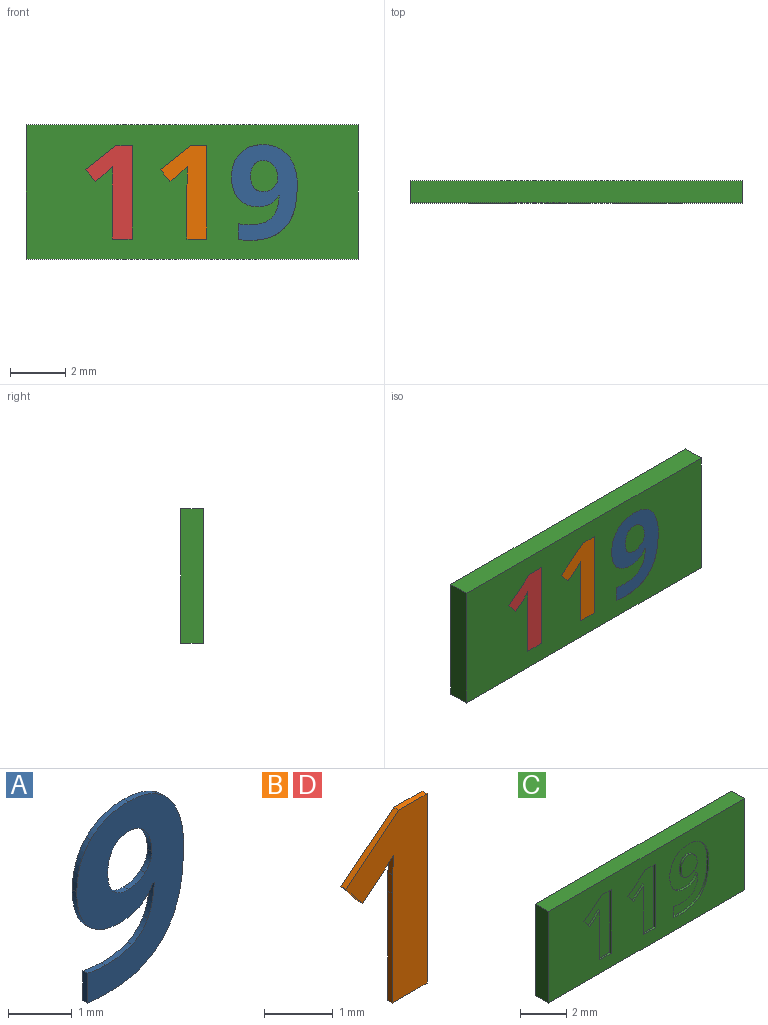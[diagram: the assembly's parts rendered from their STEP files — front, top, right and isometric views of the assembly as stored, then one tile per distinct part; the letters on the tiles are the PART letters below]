
ASSEMBLY  parts=4 mates=3
PART A: 28 faces, bbox 2.4x0.1x3.5 mm
  f0: plane 3.46x2.38mm, normal (0,-1,0), area 4.8mm2, adj f1,f2,f3,f4,f5,f6,f7,f8
  f1: extruded ~0.51x0.43mm, area 0.1mm2, adj f0,f2,f21,f23
  f2: extruded ~0.65x0.18mm, area 0.1mm2, adj f0,f1,f3,f21
  f3: extruded ~0.84x0.31mm, area 0.1mm2, adj f0,f2,f4,f21
  f4: extruded ~0.86x0.31mm, area 0.1mm2, adj f0,f3,f5,f21
  f5: extruded ~0.78x0.25mm, area 0.1mm2, adj f0,f4,f6,f21
  f6: extruded ~0.69x0.28mm, area 0.1mm2, adj f0,f5,f7,f21
  f7: extruded ~0.44x0.1mm, area 0mm2, adj f0,f6,f8,f21
  f8: extruded ~0.31x0.3mm, area 0mm2, adj f0,f7,f9,f21
  f9: plane 0.1x0.03mm, normal (0,0,-1), area 0mm2, adj f0,f8,f10,f21
  f10: extruded ~0.62x0.14mm, area 0.1mm2, adj f0,f9,f11,f21
  f11: extruded ~0.35x0.33mm, area 0mm2, adj f0,f10,f12,f21
  f12: extruded ~0.59x0.1mm, area 0.1mm2, adj f0,f11,f13,f21
  f13: extruded ~0.41x0.1mm, area 0mm2, adj f0,f12,f14,f21
  f14: plane 0.57x0.1mm, normal (-1,0,0), area 0.1mm2, adj f0,f13,f15,f21
  f15: extruded ~0.45x0.1mm, area 0mm2, adj f0,f14,f21,f22
  f16: extruded ~0.46x0.14mm, area 0mm2, adj f0,f17,f21,f26
  f17: extruded ~0.33x0.15mm, area 0mm2, adj f0,f16,f18,f21
  f18: extruded ~0.37x0.14mm, area 0mm2, adj f0,f17,f19,f21
  f19: extruded ~0.34x0.14mm, area 0mm2, adj f0,f18,f20,f21
  f20: extruded ~0.39x0.11mm, area 0mm2, adj f0,f19,f21,f25
  f21: plane 3.46x2.38mm, normal (0,1,0), area 4.8mm2, adj f1,f2,f3,f4,f5,f6,f7,f8
  f22: extruded ~1.27x0.49mm, area 0.1mm2, adj f0,f15,f21,f24
  f23: extruded ~0.79x0.15mm, area 0.1mm2, adj f0,f1,f21,f24
  f24: extruded ~1.49x0.42mm, area 0.2mm2, adj f0,f21,f22,f23
  f25: extruded ~0.44x0.12mm, area 0mm2, adj f0,f20,f21,f27
  f26: extruded ~0.37x0.19mm, area 0mm2, adj f0,f16,f21,f27
  f27: extruded ~0.35x0.15mm, area 0mm2, adj f0,f21,f25,f26
PART B: 12 faces, bbox 1.7x0.1x3.4 mm
  f0: plane 3.37x1.67mm, normal (0,-1,0), area 2.9mm2, adj f1,f2,f3,f4,f5,f6,f7,f9
  f1: plane 0.59x0.1mm, normal (0,0,1), area 0.1mm2, adj f0,f2,f8,f10
  f2: plane 1.09x0.86mm, normal (-0.62,0,0.78), area 0.1mm2, adj f0,f1,f3,f8
  f3: plane 0.43x0.34mm, normal (-0.78,0,-0.63), area 0.1mm2, adj f0,f2,f4,f8
  f4: plane 0.39x0.31mm, normal (0.63,0,-0.78), area 0mm2, adj f0,f3,f5,f8
  f5: extruded ~0.25x0.23mm, area 0mm2, adj f0,f4,f6,f8
  f6: plane 0.35x0.1mm, normal (-1,0,0.03), area 0mm2, adj f0,f5,f7,f8
  f7: plane 0.32x0.1mm, normal (-1,0,0.02), area 0mm2, adj f0,f6,f8,f9
  f8: plane 3.37x1.67mm, normal (0,1,0), area 2.9mm2, adj f1,f2,f3,f4,f5,f6,f7,f9
  f9: plane 1.95x0.1mm, normal (-1,0,0), area 0.2mm2, adj f0,f7,f8,f11
  f10: plane 3.37x0.1mm, normal (1,0,0), area 0.3mm2, adj f0,f1,f8,f11
  f11: plane 0.71x0.1mm, normal (0,0,-1), area 0.1mm2, adj f0,f8,f9,f10
PART C: 56 faces, bbox 12x0.8x4.9 mm
  f0: plane 12x4.85mm, normal (0,-1,0), area 46.6mm2, adj f1,f2,f3,f4,f6,f7,f8,f9
  f1: plane 12x0.8mm, normal (0,0,-1), area 9.6mm2, adj f0,f2,f4,f5
  f2: plane 4.85x0.8mm, normal (1,0,0), area 3.9mm2, adj f0,f1,f3,f5
  f3: plane 12x0.8mm, normal (0,0,1), area 9.6mm2, adj f0,f2,f4,f5
  f4: plane 4.85x0.8mm, normal (-1,0,0), area 3.9mm2, adj f0,f1,f3,f5
  f5: plane 12x4.85mm, normal (0,1,0), area 58.2mm2, adj f1,f2,f3,f4
  f6: extruded ~0.79x0.15mm, area 0.1mm2, adj f0,f7,f31,f32
  f7: extruded ~0.51x0.43mm, area 0.1mm2, adj f0,f6,f8,f32
  f8: extruded ~0.65x0.18mm, area 0.1mm2, adj f0,f7,f9,f32
  f9: extruded ~0.84x0.31mm, area 0.1mm2, adj f0,f8,f10,f32
  f10: extruded ~0.86x0.31mm, area 0.1mm2, adj f0,f9,f11,f32
  f11: extruded ~0.78x0.25mm, area 0.1mm2, adj f0,f10,f12,f32
  f12: extruded ~0.69x0.28mm, area 0.1mm2, adj f0,f11,f13,f32
  f13: extruded ~0.44x0.1mm, area 0mm2, adj f0,f12,f14,f32
  f14: extruded ~0.31x0.3mm, area 0mm2, adj f0,f13,f15,f32
  f15: plane 0.1x0.03mm, normal (0,0,1), area 0mm2, adj f0,f14,f16,f32
  f16: extruded ~0.62x0.14mm, area 0.1mm2, adj f0,f15,f17,f32
  f17: extruded ~0.35x0.33mm, area 0mm2, adj f0,f16,f18,f32
  f18: extruded ~0.59x0.1mm, area 0.1mm2, adj f0,f17,f19,f32
  f19: extruded ~0.41x0.1mm, area 0mm2, adj f0,f18,f20,f32
  f20: plane 0.57x0.1mm, normal (1,0,0), area 0.1mm2, adj f0,f19,f21,f32
  f21: extruded ~0.45x0.1mm, area 0mm2, adj f0,f20,f22,f32
  f22: extruded ~1.27x0.49mm, area 0.1mm2, adj f0,f21,f31,f32
  f23: extruded ~0.37x0.19mm, area 0mm2, adj f24,f30,f32,f33
  f24: extruded ~0.46x0.14mm, area 0mm2, adj f23,f25,f32,f33
  f25: extruded ~0.33x0.15mm, area 0mm2, adj f24,f26,f32,f33
  f26: extruded ~0.37x0.14mm, area 0mm2, adj f25,f27,f32,f33
  f27: extruded ~0.34x0.14mm, area 0mm2, adj f26,f28,f32,f33
  f28: extruded ~0.39x0.11mm, area 0mm2, adj f27,f29,f32,f33
  f29: extruded ~0.44x0.12mm, area 0mm2, adj f28,f30,f32,f33
  f30: extruded ~0.35x0.15mm, area 0mm2, adj f23,f29,f32,f33
  f31: extruded ~1.49x0.42mm, area 0.2mm2, adj f0,f6,f22,f32
  f32: plane 3.46x2.38mm, normal (0,-1,0), area 4.8mm2, adj f6,f7,f8,f9,f10,f11,f12,f13
  f33: plane 1.12x0.98mm, normal (0,-1,0), area 0.9mm2, adj f23,f24,f25,f26,f27,f28,f29,f30
  f34: plane 3.37x0.1mm, normal (-1,0,0), area 0.3mm2, adj f0,f35,f43,f44
  f35: plane 0.59x0.1mm, normal (0,0,-1), area 0.1mm2, adj f0,f34,f36,f44
  f36: plane 1.09x0.86mm, normal (0.62,0,-0.78), area 0.1mm2, adj f0,f35,f37,f44
  f37: plane 0.43x0.34mm, normal (0.78,0,0.63), area 0.1mm2, adj f0,f36,f38,f44
  f38: plane 0.39x0.31mm, normal (-0.63,0,0.78), area 0mm2, adj f0,f37,f39,f44
  f39: extruded ~0.25x0.23mm, area 0mm2, adj f0,f38,f40,f44
  f40: plane 0.35x0.1mm, normal (1,0,-0.03), area 0mm2, adj f0,f39,f41,f44
  f41: plane 0.32x0.1mm, normal (1,0,-0.02), area 0mm2, adj f0,f40,f42,f44
  f42: plane 1.95x0.1mm, normal (1,0,0), area 0.2mm2, adj f0,f41,f43,f44
  f43: plane 0.71x0.1mm, normal (0,0,1), area 0.1mm2, adj f0,f34,f42,f44
  f44: plane 3.37x1.67mm, normal (0,-1,0), area 2.9mm2, adj f34,f35,f36,f37,f38,f39,f40,f41
  f45: plane 3.37x0.1mm, normal (-1,0,0), area 0.3mm2, adj f0,f46,f54,f55
  f46: plane 0.59x0.1mm, normal (0,0,-1), area 0.1mm2, adj f0,f45,f47,f55
  f47: plane 1.09x0.86mm, normal (0.62,0,-0.78), area 0.1mm2, adj f0,f46,f48,f55
  f48: plane 0.43x0.34mm, normal (0.78,0,0.63), area 0.1mm2, adj f0,f47,f49,f55
  f49: plane 0.39x0.31mm, normal (-0.63,0,0.78), area 0mm2, adj f0,f48,f50,f55
  f50: extruded ~0.25x0.23mm, area 0mm2, adj f0,f49,f51,f55
  f51: plane 0.35x0.1mm, normal (1,0,-0.03), area 0mm2, adj f0,f50,f52,f55
  f52: plane 0.32x0.1mm, normal (1,0,-0.02), area 0mm2, adj f0,f51,f53,f55
  f53: plane 1.95x0.1mm, normal (1,0,0), area 0.2mm2, adj f0,f52,f54,f55
  f54: plane 0.71x0.1mm, normal (0,0,1), area 0.1mm2, adj f0,f45,f53,f55
  f55: plane 3.37x1.67mm, normal (0,-1,0), area 2.9mm2, adj f45,f46,f47,f48,f49,f50,f51,f52
PART D: same geometry as B
PLACE A t=(1.13,0.37,-0.05)mm
PLACE B t=(-1.86,0.37,-0.05)mm
PLACE C t=(0,0.37,-0.05)mm
PLACE D t=(-4.55,0.37,-0.05)mm
MATE fastened B.f0 <-> C.f0  axis (0,-1,0) through (-0.18,-0.43,-1.75)mm
MATE fastened D.f0 <-> C.f0  axis (0,-1,0) through (-2.88,-0.43,-1.75)mm
MATE fastened A.f0 <-> C.f0  axis (0,-1,0) through (1.66,-0.43,-1.76)mm
